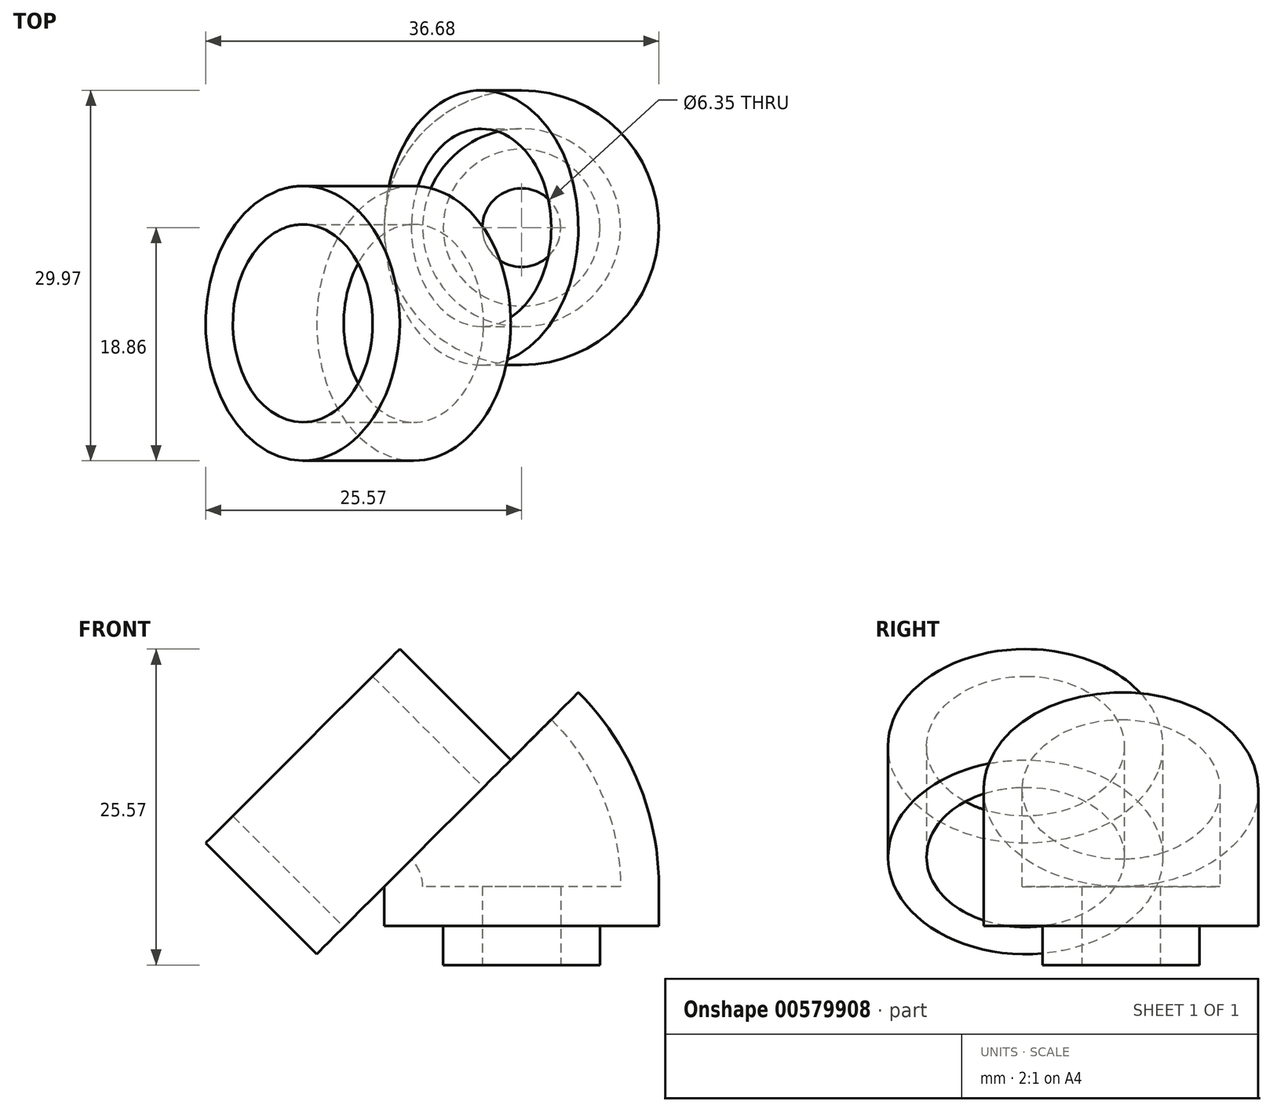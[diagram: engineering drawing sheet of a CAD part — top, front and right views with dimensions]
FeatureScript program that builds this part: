
annotation { "Feature Type Name" : "Feature", "Feature Type Description" : "" }
export const myFeature = defineFeature(function(context is Context, id is Id, definition is map)
    precondition{}
    {
        {
            var Q0;
            Q0=qCreatedBy(makeId("Top.planeOp"),FACE);
            var sketch = newSketch(context, id + "F0", { "sketchPlane" : qUnion([Q0])});
            skCircle(sketch, "E0", {"center": v(0, 0) * mm, "radius": 3.18 * mm});
            skCircle(sketch, "E1", {"center": v(0, 0) * mm, "radius": 6.35 * mm});
            skSolve(sketch);
        }
        {
            var Q0;
            Q0=qSketchRegion(id+"F0",true);
            extrude(context, id + "F1", {"entities" : qUnion([Q0]), "depth" : 3.17 * mm, "offsetDistance" : 25.4 * mm});
        }
        {
            var Q0;
            Q0=makeQuery(id+"F1.opExtrude","CAP_FACE",FACE,{"disambiguationData":[OSD([sQuery(id+"F0.wireOp",EDGE,"E0"),sQuery(id+"F0.wireOp",EDGE,"E1")])],"isStart":false});
            var sketch = newSketch(context, id + "F2", { "sketchPlane" : qUnion([Q0])});
            skCircle(sketch, "E2", {"center": v(0, 0) * mm, "radius": 11.11 * mm});
            skCircle(sketch, "E3", {"center": v(0, 0) * mm, "radius": 3.18 * mm});
            skSolve(sketch);
        }
        {
            var Q0;
            Q0=qSketchRegion(id+"F2",true);
            extrude(context, id + "F3", {"entities" : qUnion([Q0]), "operationType" : NewBodyOperationType.ADD, "depth" : 3.17 * mm, "offsetDistance" : 25.4 * mm});
        }
        {
            var Q0;
            Q0=makeQuery(id+"F3.opExtrude","CAP_FACE",FACE,{"disambiguationData":[OSD([sQuery(id+"F2.wireOp",EDGE,"E2"),sQuery(id+"F2.wireOp",EDGE,"E3")])],"isStart":false});
            var sketch = newSketch(context, id + "F4", { "sketchPlane" : qUnion([Q0])});
            skCircle(sketch, "E4", {"center": v(0, 0) * mm, "radius": 8 * mm});
            skCircle(sketch, "E5", {"center": v(0, 0) * mm, "radius": 11.11 * mm});
            skLineSegment(sketch, "E6", {"start": v(-11.11, 9.62) * mm, "end": v(-11.11, -13.9) * mm});
            skSolve(sketch);
        }
        {
            var Q0;
            Q0=qSketchRegion(id+"F4",true);
            var Q1;
            Q1=sQuery(id+"F4.wireOp",EDGE,"E6");
            revolve(context, id + "F5", {"operationType" : NewBodyOperationType.ADD, "entities" : qUnion([Q0]), "axis" : qUnion([Q1]), "revolveType" : RevolveType.ONE_DIRECTION, "angle" : 45 * degree});
        }
        {
            var Q0;
            Q0=makeQuery(id+"F5.opRevolve","CAP_FACE",FACE,{"disambiguationData":[OSD([sQuery(id+"F4.wireOp",EDGE,"E4"),sQuery(id+"F4.wireOp",EDGE,"E5")])],"isStart":false});
            var sketch = newSketch(context, id + "F6", { "sketchPlane" : qUnion([Q0])});
            skCircle(sketch, "E7", {"center": v(7.74, 0) * mm, "radius": 8 * mm});
            skCircle(sketch, "E8", {"center": v(7.74, 0) * mm, "radius": 11.11 * mm});
            skSolve(sketch);
        }
        {
            var Q0;
            Q0=qSketchRegion(id+"F6",true);
            extrude(context, id + "F7", {"entities" : qUnion([Q0]), "operationType" : NewBodyOperationType.ADD, "depth" : 12.7 * mm, "offsetDistance" : 25.4 * mm});
        }
    });
